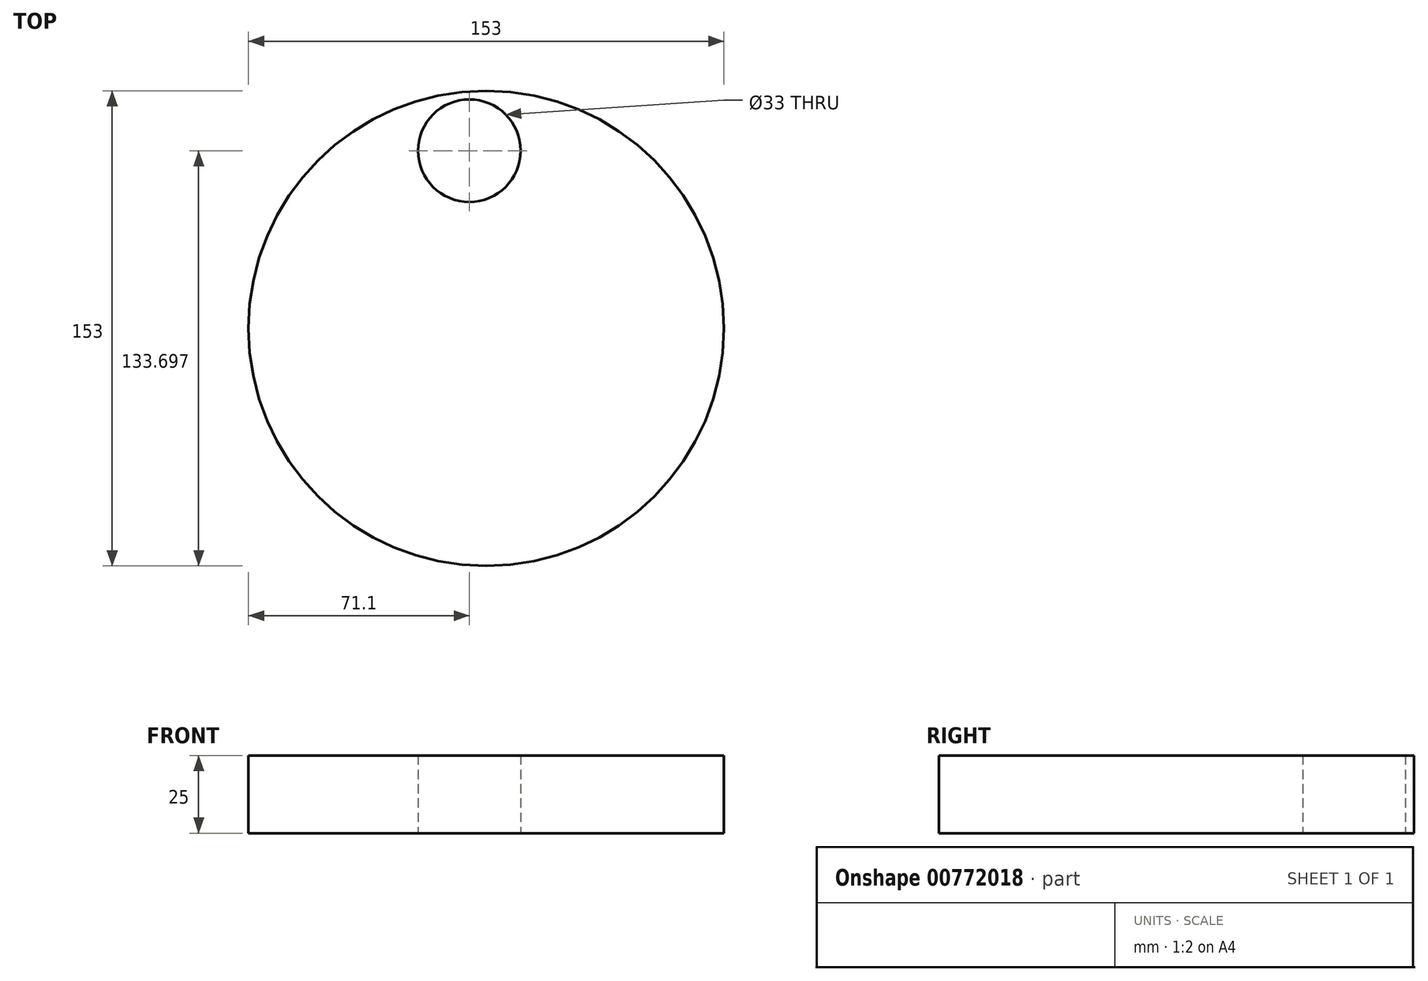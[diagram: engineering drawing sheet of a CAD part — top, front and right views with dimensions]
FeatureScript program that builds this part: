
annotation { "Feature Type Name" : "Feature", "Feature Type Description" : "" }
export const myFeature = defineFeature(function(context is Context, id is Id, definition is map)
    precondition{}
    {
        {
            var Q0;
            Q0=qCreatedBy(makeId("Top.planeOp"),FACE);
            var sketch = newSketch(context, id + "F0", { "sketchPlane" : qUnion([Q0])});
            skCircle(sketch, "E0", {"center": v(0, 0) * mm, "radius": 76.5 * mm});
            skCircle(sketch, "E1", {"center": v(-5.4, 57.2) * mm, "radius": 16.5 * mm});
            skSolve(sketch);
        }
        {
            var Q0;
            Q0=makeQuery(id+"F0.imprint","IMPRINT",FACE,{"disambiguationData":[TD([[makeQuery(id+"F0.imprint","IMPRINT",EDGE,{"derivedFrom":sQuery(id+"F0.wireOp",EDGE,"E0")}),1.0]])]});
            extrude(context, id + "F1", {"entities" : qUnion([Q0]), "depth" : 25 * mm, "offsetDistance" : 25 * mm});
        }
    });
